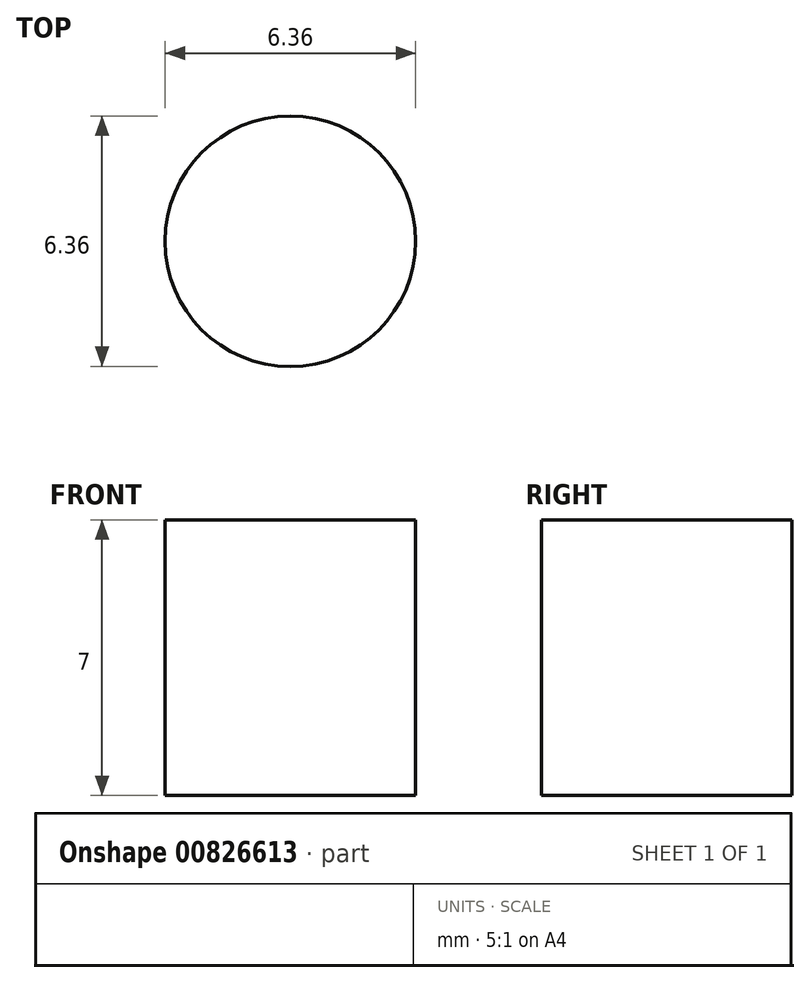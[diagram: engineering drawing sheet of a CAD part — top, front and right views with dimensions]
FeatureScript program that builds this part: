
annotation { "Feature Type Name" : "Feature", "Feature Type Description" : "" }
export const myFeature = defineFeature(function(context is Context, id is Id, definition is map)
    precondition{}
    {
        {
            var Q0;
            Q0=qCreatedBy(makeId("Front.planeOp"),FACE);
            var sketch = newSketch(context, id + "F0", { "sketchPlane" : qUnion([Q0])});
            skLineSegment(sketch, "E0", {"start": v(8, 7) * mm, "end": v(8, 0) * mm, "construction": true});
            skLineSegment(sketch, "E1", {"start": v(8, 7) * mm, "end": v(3.18, 7) * mm});
            skLineSegment(sketch, "E2", {"start": v(3.18, 7) * mm, "end": v(3.18, 0) * mm});
            skLineSegment(sketch, "E3", {"start": v(3.18, 0) * mm, "end": v(8, 0) * mm});
            skPoint(sketch, "E4", {"position": v(8, 3.5) * mm});
            skLineSegment(sketch, "E5", {"start": v(8, 0) * mm, "end": v(8, -1.75) * mm});
            skLineSegment(sketch, "E6", {"start": v(3.18, 7) * mm, "end": v(2.43, 7) * mm, "construction": true});
            skLineSegment(sketch, "E7", {"start": v(2.43, 7) * mm, "end": v(2.43, 0) * mm, "construction": true});
            skLineSegment(sketch, "E8", {"start": v(2.43, 0) * mm, "end": v(3.18, 0) * mm, "construction": true});
            skLineSegment(sketch, "E9", {"start": v(3.18, 7) * mm, "end": v(2.58, 7) * mm});
            skLineSegment(sketch, "E10", {"start": v(2.58, 7) * mm, "end": v(0, 7) * mm});
            skLineSegment(sketch, "E11", {"start": v(3.18, 0) * mm, "end": v(0, 0) * mm});
            skLineSegment(sketch, "E12", {"start": v(0, 7) * mm, "end": v(0, 0) * mm});
            skSolve(sketch);
        }
        {
            var Q0;
            Q0 = qSketchRegion(id + "F0", true);
            var Q1;
            Q1=sQuery(id+"F0.wireOp",EDGE,"E12");
            revolve(context, id + "F1", {"surfaceOperationType" : NewSurfaceOperationType.NEW, "entities" : qUnion([Q0]), "axis" : qUnion([Q1]), "revolveType" : RevolveType.FULL});
        }
    });
